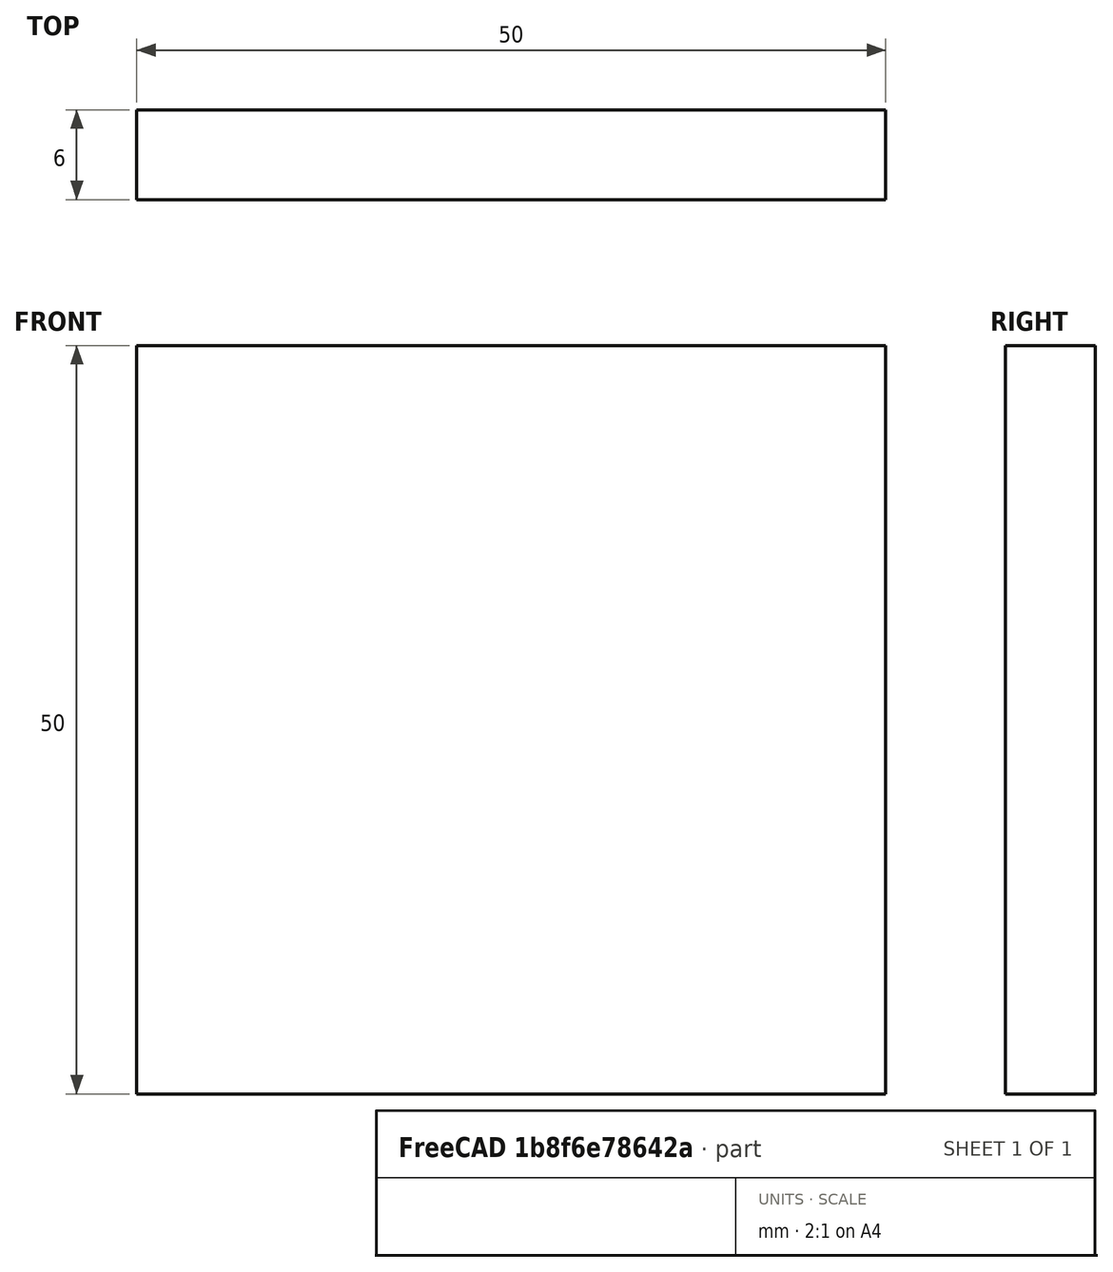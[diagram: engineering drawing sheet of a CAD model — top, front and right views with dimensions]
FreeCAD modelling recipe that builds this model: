
FCSTD DOCUMENT  (FreeCAD 0.15R4671 (Git))
Label: Flat Bar 50x6 EN10058 S235JR
License: All rights reserved
LicenseURL: http://en.wikipedia.org/wiki/All_rights_reserved
objects: Sketcher::SketchObject×1, Part::Extrusion×1
note: 2 computed .brp shape members not serialized (recipe doc carries the construction recipe); baked Part::Feature solids carry a one-line shape summary decoded from their .brp

FEATURE [Sketcher::SketchObject] Sketch
  sketch-geometry (4):
    g0: LineSegment StartX=-25 StartY=-3 StartZ=0 EndX=25 EndY=-3 EndZ=0
    g1: LineSegment StartX=25 StartY=-3 StartZ=0 EndX=25 EndY=3 EndZ=0
    g2: LineSegment StartX=25 StartY=3 StartZ=0 EndX=-25 EndY=3 EndZ=0
    g3: LineSegment StartX=-25 StartY=3 StartZ=0 EndX=-25 EndY=-3 EndZ=0
  constraints (12):
    c: Coincident(g0,g1)
    c: Coincident(g1,g2)
    c: Coincident(g2,g3)
    c: Coincident(g3,g0)
    c: Horizontal(g0)
    c: Horizontal(g2)
    c: Vertical(g1)
    c: Vertical(g3)
    c: Symmetric(g1,g2,g-2)
    c: Symmetric(g0,g1,g-1)
    c: DistanceY(g1) = 6
    c: DistanceX(g0) = 50
FEATURE [Part::Extrusion] Extrude  label="Flat Bar 50x6 EN10058 S235JR"
  Base = -> Sketch
  Dir = (0,0,50)
  Solid = true
